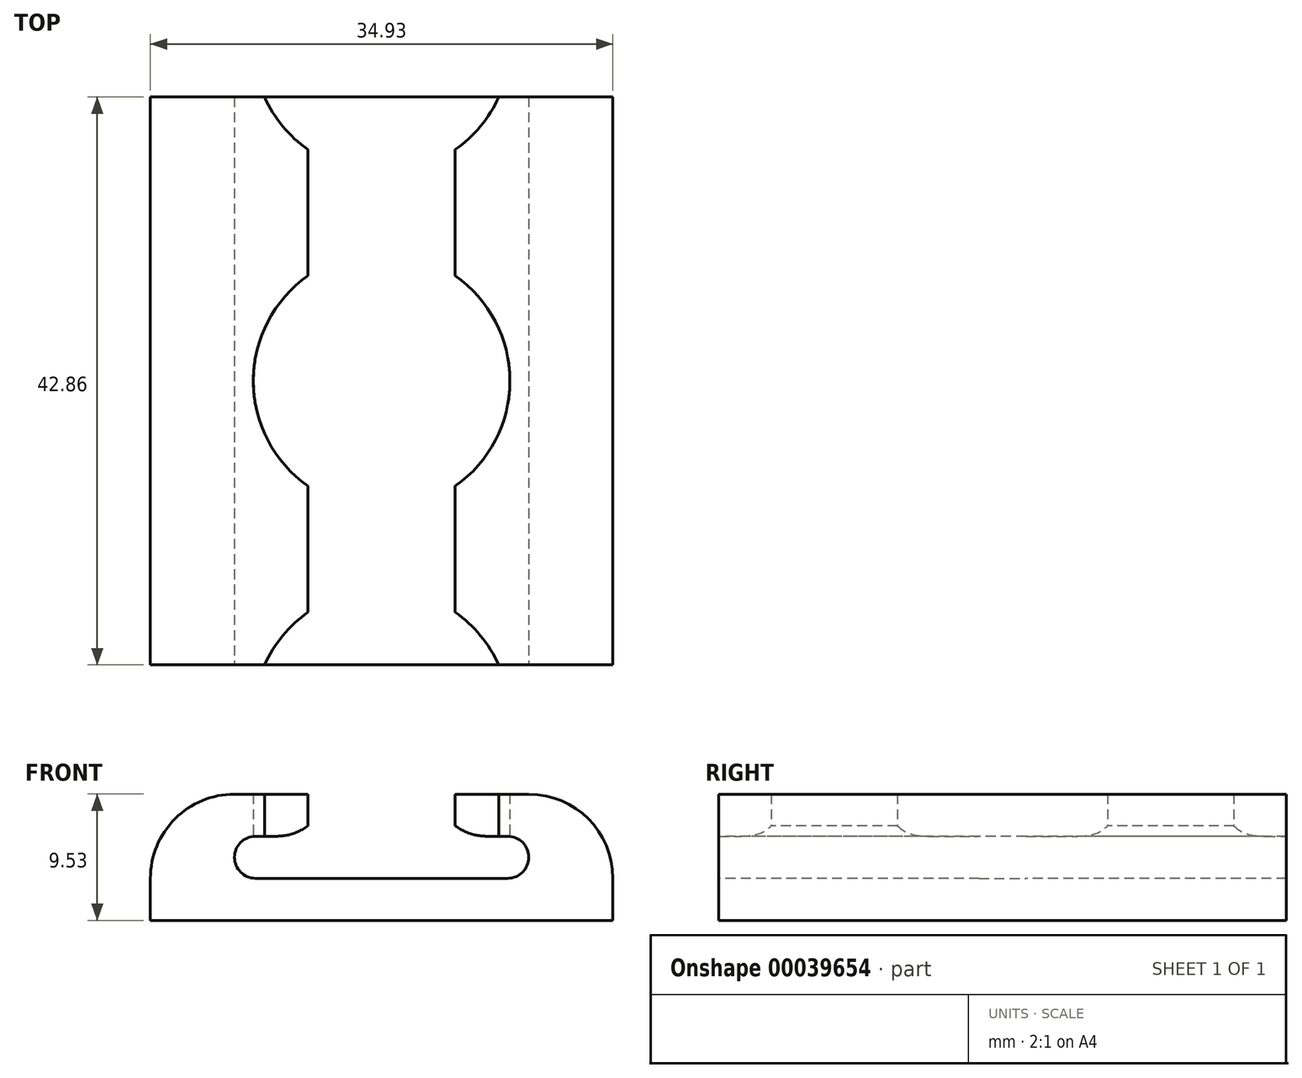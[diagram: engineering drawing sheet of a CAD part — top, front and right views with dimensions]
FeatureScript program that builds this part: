
annotation { "Feature Type Name" : "Feature", "Feature Type Description" : "" }
export const myFeature = defineFeature(function(context is Context, id is Id, definition is map)
    precondition{}
    {
        {
            var Q0;
            Q0=qCreatedBy(makeId("Top.planeOp"),FACE);
            var sketch = newSketch(context, id + "F0", { "sketchPlane" : qUnion([Q0])});
            skLineSegment(sketch, "E0", {"start": v(0, 0) * mm, "end": v(0, 9.53) * mm});
            skLineSegment(sketch, "E1", {"start": v(0, 0) * mm, "end": v(11.11, 0) * mm});
            skLineSegment(sketch, "E2", {"start": v(11.11, 0) * mm, "end": v(11.11, 9.52) * mm});
            skLineSegment(sketch, "E3", {"start": v(0, 34.92) * mm, "end": v(0, 25.4) * mm});
            skPoint(sketch, "E4.endSnap0", {"position": v(5.56, 0) * mm});
            skArc(sketch, "E5", {"start": v(0, 25.4) * mm, "mid": v(-4.13, 17.46) * mm, "end": v(0, 9.52) * mm});
            skLineSegment(sketch, "E6.trimOffspring", {"start": v(11.11, 25.4) * mm, "end": v(11.11, 34.92) * mm});
            skArc(sketch, "E7.trimOffspring", {"start": v(11.11, 9.52) * mm, "mid": v(15.25, 17.46) * mm, "end": v(11.11, 25.4) * mm});
            skLineSegment(sketch, "E8", {"start": v(0, 50.8) * mm, "end": v(0, 60.33) * mm});
            skArc(sketch, "E9", {"start": v(0, 50.8) * mm, "mid": v(-4.13, 42.86) * mm, "end": v(0, 34.92) * mm});
            skLineSegment(sketch, "E10", {"start": v(11.11, 50.8) * mm, "end": v(11.11, 60.33) * mm});
            skArc(sketch, "E11.trimOffspring", {"start": v(11.11, 34.92) * mm, "mid": v(15.25, 42.86) * mm, "end": v(11.11, 50.8) * mm});
            skArc(sketch, "E12", {"start": v(0, 76.2) * mm, "mid": v(-4.13, 68.26) * mm, "end": v(0, 60.33) * mm});
            skLineSegment(sketch, "E13", {"start": v(0, 76.2) * mm, "end": v(0, 85.73) * mm});
            skLineSegment(sketch, "E14", {"start": v(0, 85.73) * mm, "end": v(11.11, 85.73) * mm});
            skLineSegment(sketch, "E15", {"start": v(11.11, 85.73) * mm, "end": v(11.11, 76.2) * mm});
            skArc(sketch, "E16.trimOffspring", {"start": v(11.11, 60.33) * mm, "mid": v(15.25, 68.26) * mm, "end": v(11.11, 76.2) * mm});
            skLineSegment(sketch, "E17", {"start": v(5.56, 0) * mm, "end": v(23.02, 0) * mm});
            skLineSegment(sketch, "E18", {"start": v(5.56, 0) * mm, "end": v(-11.9, 0) * mm});
            skLineSegment(sketch, "E19", {"start": v(23.02, 85.73) * mm, "end": v(5.56, 85.73) * mm});
            skLineSegment(sketch, "E20", {"start": v(5.56, 85.73) * mm, "end": v(-11.9, 85.73) * mm});
            skLineSegment(sketch, "E21", {"start": v(-11.9, 85.73) * mm, "end": v(-11.9, 0) * mm});
            skLineSegment(sketch, "E22", {"start": v(-11.9, 64.3) * mm, "end": v(23.02, 64.3) * mm});
            skLineSegment(sketch, "E23", {"start": v(23.02, 21.43) * mm, "end": v(-11.9, 21.43) * mm});
            skLineSegment(sketch, "E24", {"start": v(23.02, 85.73) * mm, "end": v(23.02, 0) * mm});
            skSolve(sketch);
        }
        {
            var Q0;
            {var subQ7=sQuery(id+"F0.wireOp",EDGE,"E3");Q0=makeQuery(id+"F0.imprint","IMPRINT",FACE,{"disambiguationData":[TD([[makeQuery(id+"F0.imprint","IMPRINT",EDGE,{"derivedFrom":subQ7}),1.0]])]});}
            extrude(context, id + "F1", {"entities" : qUnion([Q0]), "depth" : 3.17 * mm});
        }
        {
            var Q0;
            {var subQ0=sQuery(id+"F0.wireOp",EDGE,"E3");Q0=makeQuery(id+"F0.imprint","IMPRINT",FACE,{"disambiguationData":[TD([[makeQuery(id+"F0.imprint","IMPRINT",EDGE,{"derivedFrom":subQ0}),-1.0]])]});}
            var Q1;
            {var subQ2=sQuery(id+"F0.wireOp",EDGE,"E6.trimOffspring");Q1=makeQuery(id+"F0.imprint","IMPRINT",FACE,{"disambiguationData":[TD([[makeQuery(id+"F0.imprint","IMPRINT",EDGE,{"derivedFrom":subQ2}),-1.0]])]});}
            extrude(context, id + "F2", {"entities" : qUnion([Q0, Q1]), "operationType" : NewBodyOperationType.ADD, "depth" : 9.52 * mm});
        }
        {
            var Q0;
            Q0=qCreatedBy(makeId("Front.planeOp"),FACE);
            var sketch = newSketch(context, id + "F3", { "sketchPlane" : qUnion([Q0])});
            skLineSegment(sketch, "E25", {"start": v(-3.97, 6.35) * mm, "end": v(-2.38, 6.35) * mm});
            skLineSegment(sketch, "E26", {"start": v(0, 6.35) * mm, "end": v(0, 3.18) * mm});
            skLineSegment(sketch, "E27", {"start": v(0, 3.18) * mm, "end": v(-3.97, 3.18) * mm});
            skArc(sketch, "E28", {"start": v(-3.97, 6.35) * mm, "mid": v(-5.56, 4.76) * mm, "end": v(-3.97, 3.18) * mm});
            skPoint(sketch, "E28.centerSnap0", {"position": v(-5.56, 4.76) * mm});
            skLineSegment(sketch, "E29", {"start": v(0, 6.35) * mm, "end": v(0, 7.14) * mm});
            skArc(sketch, "E30", {"start": v(-2.38, 6.35) * mm, "mid": v(-1.13, 6.55) * mm, "end": v(0, 7.14) * mm});
            skLineSegment(sketch, "E31", {"start": v(0, 3.18) * mm, "end": v(11.11, 3.18) * mm});
            skLineSegment(sketch, "E32.MirrorCS", {"start": v(11.11, 6.35) * mm, "end": v(11.11, 3.18) * mm});
            skLineSegment(sketch, "E33.MirrorCS", {"start": v(11.11, 6.35) * mm, "end": v(11.11, 7.14) * mm});
            skArc(sketch, "E34.MirrorCS", {"start": v(13.5, 6.35) * mm, "mid": v(12.24, 6.55) * mm, "end": v(11.11, 7.14) * mm});
            skLineSegment(sketch, "E35.MirrorCS", {"start": v(15.08, 6.35) * mm, "end": v(13.5, 6.35) * mm});
            skArc(sketch, "E36.MirrorCS", {"start": v(15.08, 6.35) * mm, "mid": v(16.67, 4.76) * mm, "end": v(15.08, 3.18) * mm});
            skLineSegment(sketch, "E37.MirrorCS", {"start": v(11.11, 3.18) * mm, "end": v(15.08, 3.18) * mm});
            skLineSegment(sketch, "E38", {"start": v(0, 7.14) * mm, "end": v(11.11, 7.14) * mm});
            skSolve(sketch);
        }
        {
            var Q0;
            Q0=makeQuery(id+"F3.imprint","IMPRINT",FACE,{"disambiguationData":[TD([[makeQuery(id+"F3.imprint","IMPRINT",EDGE,{"derivedFrom":sQuery(id+"F3.wireOp",EDGE,"E25")}),-1.0]])]});
            var Q1;
            {var subQ0=sQuery(id+"F3.wireOp",EDGE,"bd1d0551-0bfa-4911-9c7f-cf31212506f1");Q1=makeQuery(id+"F3.imprint","IMPRINT",FACE,{"disambiguationData":[TD([[makeQuery(id+"F3.imprint","IMPRINT",EDGE,{"derivedFrom":subQ0}),1.0]])]});}
            var Q2;
            Q2=makeQuery(id+"F3.imprint","IMPRINT",FACE,{"disambiguationData":[TD([[makeQuery(id+"F3.imprint","IMPRINT",EDGE,{"derivedFrom":sQuery(id+"F3.wireOp",EDGE,"E32.MirrorCS")}),1.0]])]});
            extrude(context, id + "F4", {"entities" : qUnion([Q0, Q1, Q2]), "operationType" : NewBodyOperationType.REMOVE, "oppositeDirection" : true, "depth" : 85.72 * mm});
        }
        {
            var Q0;
            Q0=makeQuery(id+"F2.opExtrude","CAP_EDGE",EDGE,{"disambiguationData":[OSD([sQuery(id+"F0.wireOp",EDGE,"E24")])],"isStart":false});
            var Q1;
            Q1=makeQuery(id+"F2.opExtrude","CAP_EDGE",EDGE,{"disambiguationData":[OSD([sQuery(id+"F0.wireOp",EDGE,"E21")])],"isStart":false});
            fillet(context, id + "F5", {"entities" : qUnion([Q0, Q1]), "radius" : 6.35 * mm, "tangentPropagation" : true, "allowEdgeOverflow" : false});
        }
    });
